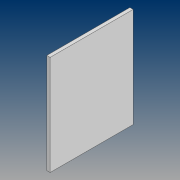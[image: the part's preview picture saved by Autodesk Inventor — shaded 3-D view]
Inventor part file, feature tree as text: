
AUTODESK INVENTOR PART (.ipt)
format: ipt  version: 2021 (Build 250183000, 183)  size: 77,824 bytes
history: native  units: mm
features: extrude x1, sketch x1
ambient origin geometry x8: Origin, YZ Plane, XZ Plane, XY Plane, X Axis, Y Axis, Z Axis, Center Point
bodies: Solid1 (feature_tree)
feature tree (2):
  extrude  "Extrusion1"  Depth=300.0mm
  sketch  "Sketch1"  dims[d0=250.0mm d1=300.0mm d2=10.0mm d3=0.0mm]
